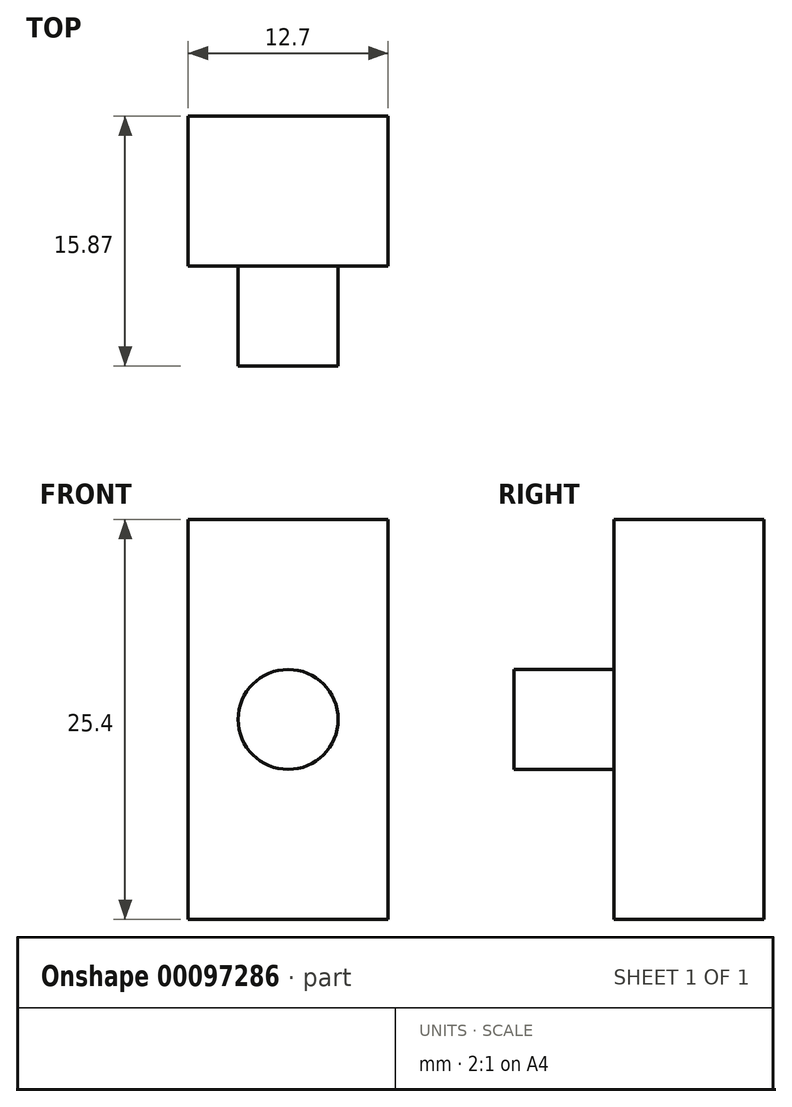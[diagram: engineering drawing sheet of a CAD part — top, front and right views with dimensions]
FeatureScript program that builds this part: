
annotation { "Feature Type Name" : "Feature", "Feature Type Description" : "" }
export const myFeature = defineFeature(function(context is Context, id is Id, definition is map)
    precondition{}
    {
        {
            var Q0;
            Q0=qCreatedBy(makeId("Front.planeOp"),FACE);
            var sketch = newSketch(context, id + "F0", { "sketchPlane" : qUnion([Q0])});
            skLineSegment(sketch, "E0.bottom", {"start": v(6.35, 12.7) * mm, "end": v(-6.35, 12.7) * mm});
            skLineSegment(sketch, "E0.top", {"start": v(6.35, -12.7) * mm, "end": v(-6.35, -12.7) * mm});
            skLineSegment(sketch, "E0.left", {"start": v(6.35, 12.7) * mm, "end": v(6.35, -12.7) * mm});
            skLineSegment(sketch, "E0.right", {"start": v(-6.35, 12.7) * mm, "end": v(-6.35, -12.7) * mm});
            skPoint(sketch, "E0.middle", {"position": v(0, 0) * mm});
            skSolve(sketch);
        }
        {
            var Q0;
            Q0 = qSketchRegion(id + "F0", true);
            extrude(context, id + "F1", {"entities" : qUnion([Q0]), "endBound" : BoundingType.SYMMETRIC, "depth" : 9.52 * mm, "hasSecondDirection" : true, "secondDirectionOppositeDirection" : true, "secondDirectionDepth" : 25.4 * mm});
        }
        {
            var Q0;
            Q0=makeQuery(id+"F1.opExtrude","CAP_FACE",FACE,{"disambiguationData":[OSD([sQuery(id+"F0.wireOp",EDGE,"E0.bottom"),sQuery(id+"F0.wireOp",EDGE,"E0.top"),sQuery(id+"F0.wireOp",EDGE,"E0.left"),sQuery(id+"F0.wireOp",EDGE,"E0.right")])],"isStart":false});
            var sketch = newSketch(context, id + "F2", { "sketchPlane" : qUnion([Q0])});
            skCircle(sketch, "E1", {"center": v(0, 0) * mm, "radius": 3.17 * mm});
            skSolve(sketch);
        }
        {
            var Q0;
            Q0 = qSketchRegion(id + "F2", true);
            extrude(context, id + "F3", {"entities" : qUnion([Q0]), "operationType" : NewBodyOperationType.ADD, "depth" : 6.35 * mm});
        }
    });
